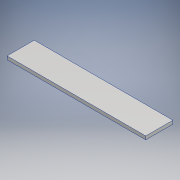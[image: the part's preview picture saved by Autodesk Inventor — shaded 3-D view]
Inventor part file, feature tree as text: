
AUTODESK INVENTOR PART (.ipt)
format: ipt  version: 2017 (Build 210142000, 142)  size: 92,160 bytes
history: native  units: mm
features: extrude x1, sketch x1
ambient origin geometry x8: Origin, YZ Plane, XZ Plane, XY Plane, X Axis, Y Axis, Z Axis, Center Point
bodies: Body1 (feature_tree)
feature tree (2):
  extrude  "Extrusion2"  Depth=76.2mm
  sketch  "Sketch1"  dims[d0=388.62mm d1=76.2mm d4=9.525mm d5=0.0mm]
